# Revit family: SLA_ALUM-FIXED
name_source: partatom
category: Windows
revit_build: Autodesk Revit 2016 (Build: 20150506_1715(x64)
units: mm (PartAtom-declared; Revit-internal decimal feet)

## family parameters
Always vertical = Yes
Cut with Voids When Loaded = No
Host = Wall
Room Calculation Point = No
Shared = No

## types (3) — shared parameters
Analytic Construction = <None>
Frame Depth = 0' - 4 7/8"
Frame Height = 0' - 2"
Wall Closure = By host

## per-type parameters (varying)
| type | Default Sill Height | Description | Frame | Glass | Height | Panel Width | Rough Height | Rough Width | Width |
| 12"w x 60" | 9' - 0" |  | Aluminum - Brushed | Glass - Clear, Grey | 1' - 6" | 2' - 3" | 1' - 6" | 5' - 0" | 5' - 0" |
| 54"w x 72"h | 5' - 0" | INTERIOR | Metal - Steel - dark | Glass Dark | 6' - 0" | 2' - 1" | 6' - 0" | 4' - 8" | 4' - 8" |
| 48"w x 48" | 3' - 0" |  | Aluminum - Brushed | Glass - Clear, Grey | 4' - 0" | 1' - 9" | 4' - 0" | 4' - 0" | 4' - 0" |

## geometry (parser evidence)
native form markers: Blend x15, Sweep x2
no freeform markers — native parametric forms only
